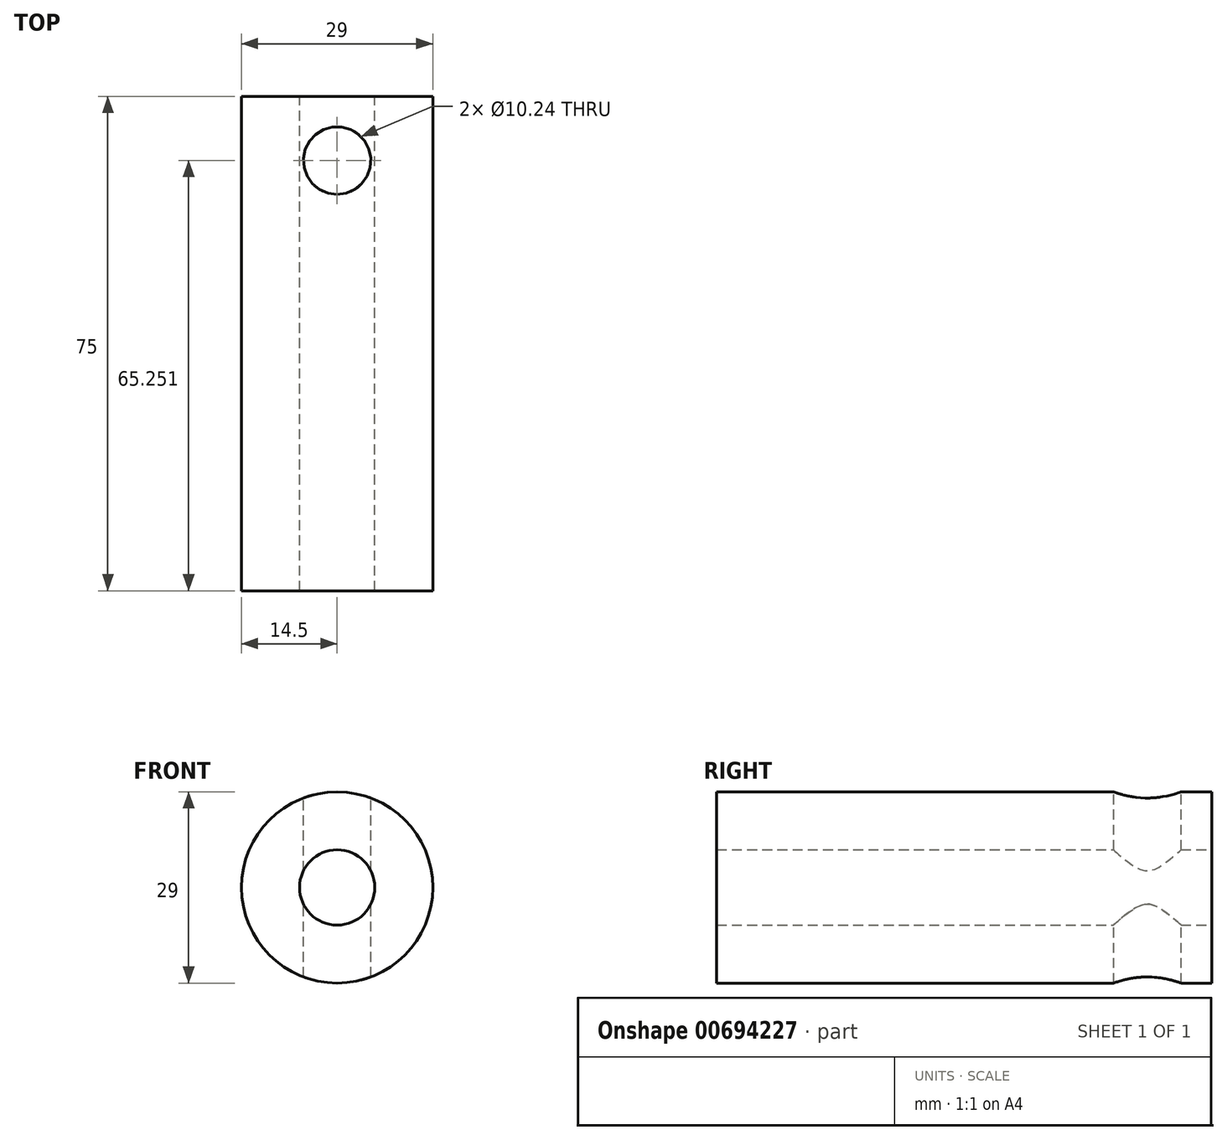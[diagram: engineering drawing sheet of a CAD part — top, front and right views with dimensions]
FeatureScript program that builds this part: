
annotation { "Feature Type Name" : "Feature", "Feature Type Description" : "" }
export const myFeature = defineFeature(function(context is Context, id is Id, definition is map)
    precondition{}
    {
        {
            var Q0;
            Q0=qCreatedBy(makeId("Front.planeOp"),FACE);
            var sketch = newSketch(context, id + "F0", { "sketchPlane" : qUnion([Q0])});
            skCircle(sketch, "E0", {"center": v(0, 0) * mm, "radius": 14.5 * mm});
            skCircle(sketch, "E1", {"center": v(0, 0) * mm, "radius": 5.7 * mm});
            skSolve(sketch);
        }
        {
            var Q0;
            Q0=makeQuery(id+"F0.imprint","IMPRINT",FACE,{"disambiguationData":[TD([[makeQuery(id+"F0.imprint","IMPRINT",EDGE,{"derivedFrom":sQuery(id+"F0.wireOp",EDGE,"E0")}),1.0]])]});
            extrude(context, id + "F1", {"entities" : qUnion([Q0]), "endBound" : BoundingType.SYMMETRIC, "depth" : 75 * mm, "offsetDistance" : 25 * mm});
        }
        {
            var Q0;
            Q0=qCreatedBy(makeId("Top.planeOp"),FACE);
            var sketch = newSketch(context, id + "F2", { "sketchPlane" : qUnion([Q0])});
            skCircle(sketch, "E2", {"center": v(0, 27.75) * mm, "radius": 5.12 * mm});
            skSolve(sketch);
        }
        {
            var Q0;
            Q0=qSketchRegion(id+"F2",true);
            extrude(context, id + "F3", {"entities" : qUnion([Q0]), "operationType" : NewBodyOperationType.REMOVE, "endBound" : BoundingType.SYMMETRIC, "oppositeDirection" : true, "depth" : 30 * mm, "offsetDistance" : 25 * mm});
        }
    });
